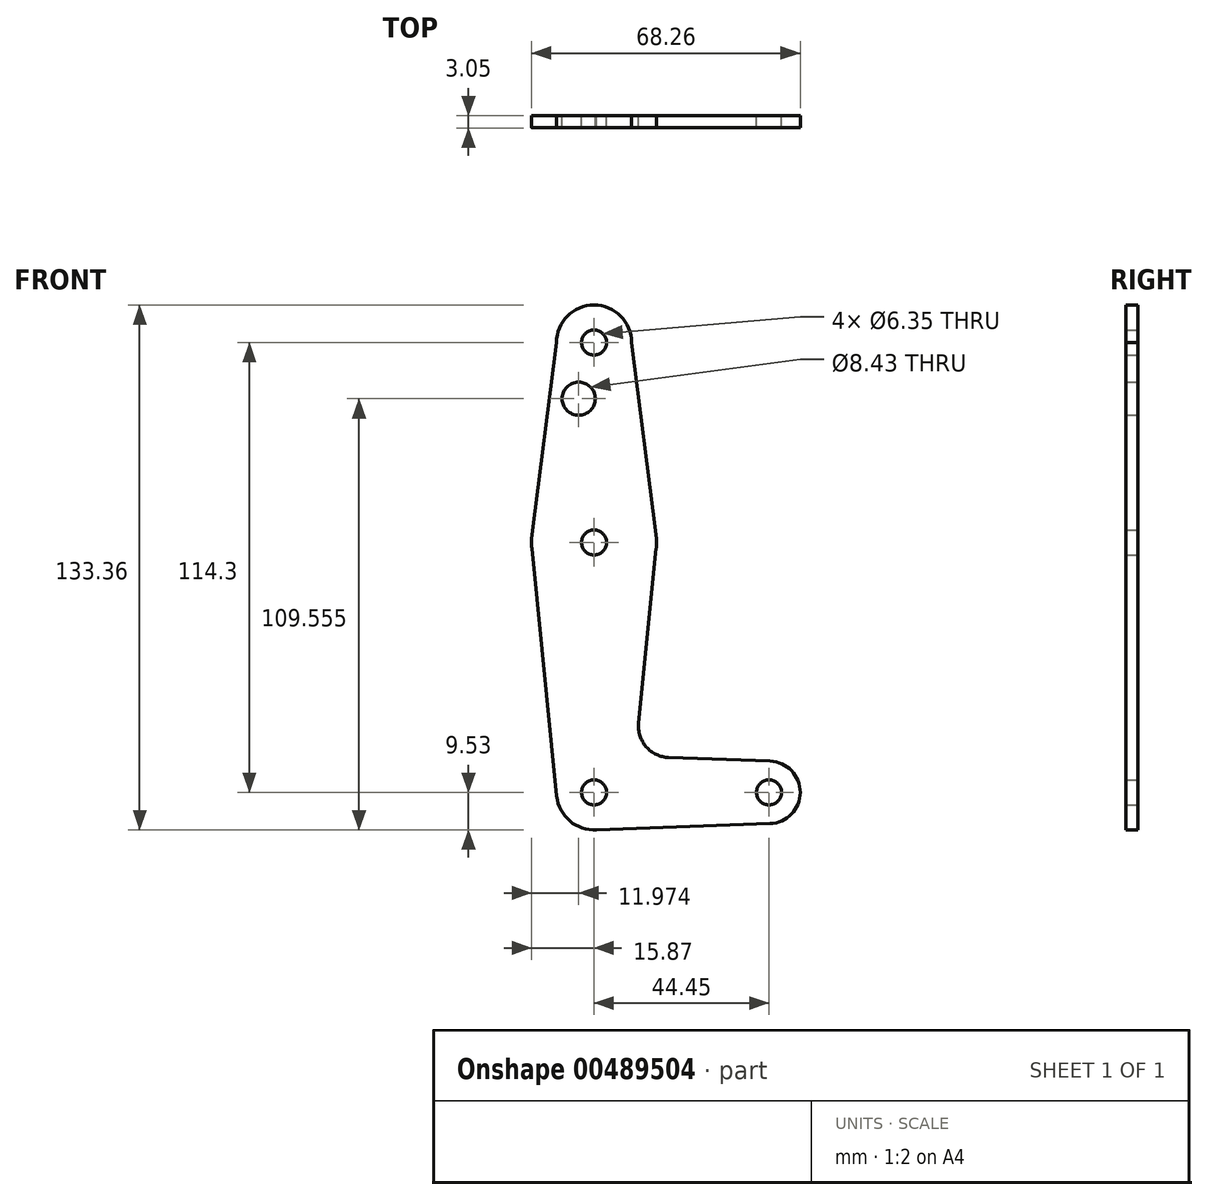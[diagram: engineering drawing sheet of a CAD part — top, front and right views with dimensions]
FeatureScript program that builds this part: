
annotation { "Feature Type Name" : "Feature", "Feature Type Description" : "" }
export const myFeature = defineFeature(function(context is Context, id is Id, definition is map)
    precondition{}
    {
        {
            var Q0;
            Q0=qCreatedBy(makeId("Front.planeOp"),FACE);
            var sketch = newSketch(context, id + "F0", { "sketchPlane" : qUnion([Q0])});
            skLineSegment(sketch, "E0", {"start": v(0, 0) * mm, "end": v(0, 114.3) * mm});
            skLineSegment(sketch, "E1", {"start": v(0, 0) * mm, "end": v(0, 63.5) * mm, "construction": true});
            skCircle(sketch, "E2", {"center": v(0, 114.3) * mm, "radius": 9.53 * mm});
            skCircle(sketch, "E3", {"center": v(0, 63.5) * mm, "radius": 15.88 * mm});
            skCircle(sketch, "E4", {"center": v(0, 0) * mm, "radius": 9.53 * mm});
            skLineSegment(sketch, "E5", {"start": v(0, 0) * mm, "end": v(44.45, 0) * mm, "construction": true});
            skCircle(sketch, "E6", {"center": v(44.45, 0) * mm, "radius": 7.94 * mm});
            skLineSegment(sketch, "E7", {"start": v(-9.53, 114.3) * mm, "end": v(-15.75, 65.5) * mm});
            skLineSegment(sketch, "E8", {"start": v(9.53, 114.3) * mm, "end": v(15.75, 65.5) * mm});
            skLineSegment(sketch, "E9", {"start": v(0, -9.53) * mm, "end": v(44.73, -7.93) * mm});
            skCircle(sketch, "E10", {"center": v(0, 114.3) * mm, "radius": 3.18 * mm});
            skLineSegment(sketch, "E11", {"start": v(-15.8, 61.91) * mm, "end": v(-9.48, -0.95) * mm});
            skCircle(sketch, "E12", {"center": v(0, 63.5) * mm, "radius": 3.18 * mm});
            skCircle(sketch, "E13", {"center": v(-3.9, 100.03) * mm, "radius": 4.21 * mm});
            skCircle(sketch, "E14", {"center": v(0, 0) * mm, "radius": 3.18 * mm});
            skCircle(sketch, "E15", {"center": v(44.45, 0) * mm, "radius": 3.18 * mm});
            skLineSegment(sketch, "E16", {"start": v(15.8, 61.91) * mm, "end": v(11.34, 17.59) * mm});
            skLineSegment(sketch, "E17", {"start": v(18.97, 8.85) * mm, "end": v(44.73, 7.93) * mm});
            skPoint(sketch, "E18.newPointA", {"position": v(9.57, 0) * mm});
            skArc(sketch, "E18.filletArc", {"start": v(11.34, 17.59) * mm, "mid": v(13.26, 11.57) * mm, "end": v(18.97, 8.85) * mm});
            skSolve(sketch);
        }
        {
            var Q0;
            Q0 = qSketchRegion(id + "F0", true);
            extrude(context, id + "F1", {"entities" : qUnion([Q0]), "depth" : 3.05 * mm});
        }
    });
